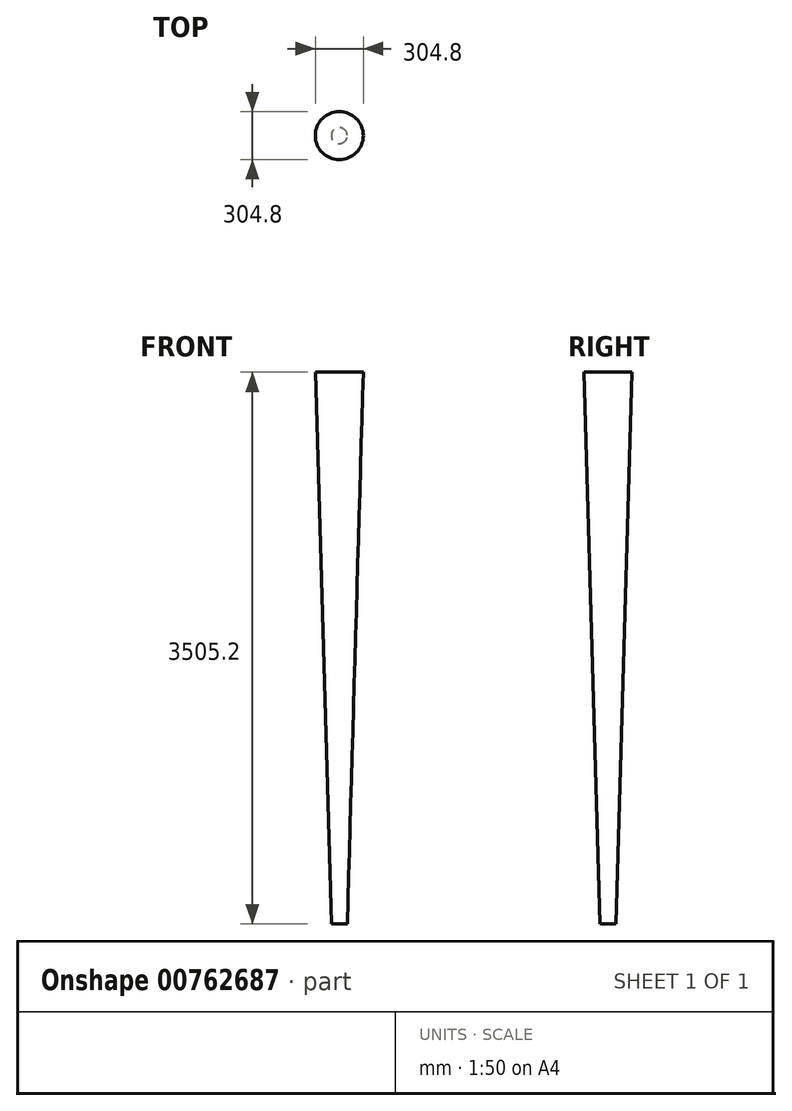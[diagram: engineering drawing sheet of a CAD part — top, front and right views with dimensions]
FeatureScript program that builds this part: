
annotation { "Feature Type Name" : "Feature", "Feature Type Description" : "" }
export const myFeature = defineFeature(function(context is Context, id is Id, definition is map)
    precondition{}
    {
        {
            var Q0;
            Q0=qCreatedBy(makeId("Front.planeOp"),FACE);
            var sketch = newSketch(context, id + "F0", { "sketchPlane" : qUnion([Q0])});
            skLineSegment(sketch, "E0", {"start": v(-5.97, 1755.4) * mm, "end": v(-5.97, -1749.8) * mm});
            skLineSegment(sketch, "E1", {"start": v(146.43, 1755.4) * mm, "end": v(44.83, -1749.74) * mm});
            skLineSegment(sketch, "E2", {"start": v(-5.97, -1749.8) * mm, "end": v(44.83, -1749.74) * mm});
            skLineSegment(sketch, "E3", {"start": v(-5.97, 1755.4) * mm, "end": v(146.43, 1755.4) * mm});
            skPoint(sketch, "E4.orphan", {"position": v(146.67, 1763.68) * mm});
            skPoint(sketch, "E5.orphan", {"position": v(146.67, 1755.4) * mm});
            skSolve(sketch);
        }
        {
            var Q0;
            Q0 = qSketchRegion(id + "F0", true);
            var Q1;
            Q1=sQuery(id+"F0.wireOp",EDGE,"E0");
            revolve(context, id + "F1", {"surfaceOperationType" : NewSurfaceOperationType.NEW, "entities" : qUnion([Q0]), "axis" : qUnion([Q1]), "revolveType" : RevolveType.FULL});
        }
    });
